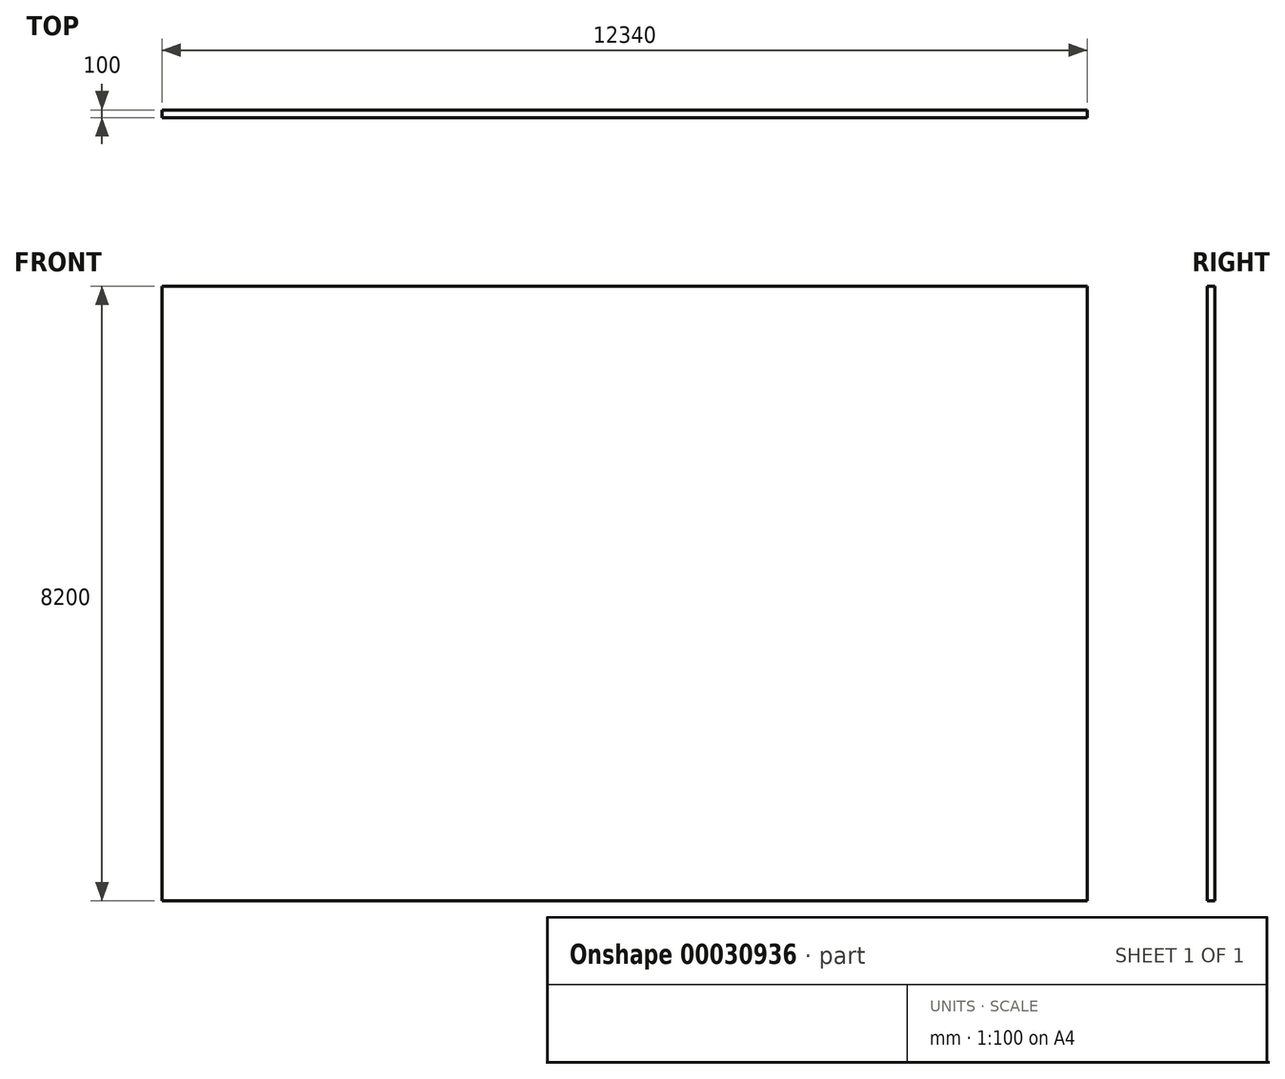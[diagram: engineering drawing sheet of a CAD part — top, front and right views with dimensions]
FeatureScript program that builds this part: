
annotation { "Feature Type Name" : "Feature", "Feature Type Description" : "" }
export const myFeature = defineFeature(function(context is Context, id is Id, definition is map)
    precondition{}
    {
        {
            var Q0;
            Q0=qCreatedBy(makeId("Top.planeOp"),FACE);
            var sketch = newSketch(context, id + "F0", { "sketchPlane" : qUnion([Q0])});
            skLineSegment(sketch, "E0.bottom", {"start": v(0, 0) * mm, "end": v(-12340, 0) * mm});
            skLineSegment(sketch, "E0.top", {"start": v(0, 100) * mm, "end": v(-12340, 100) * mm});
            skLineSegment(sketch, "E0.left", {"start": v(0, 0) * mm, "end": v(0, 100) * mm});
            skLineSegment(sketch, "E0.right", {"start": v(-12340, 0) * mm, "end": v(-12340, 100) * mm});
            skSolve(sketch);
        }
        {
            var Q0;
            Q0 = qSketchRegion(id + "F0", true);
            extrude(context, id + "F1", {"entities" : qUnion([Q0]), "depth" : 8200 * mm});
        }
    });
